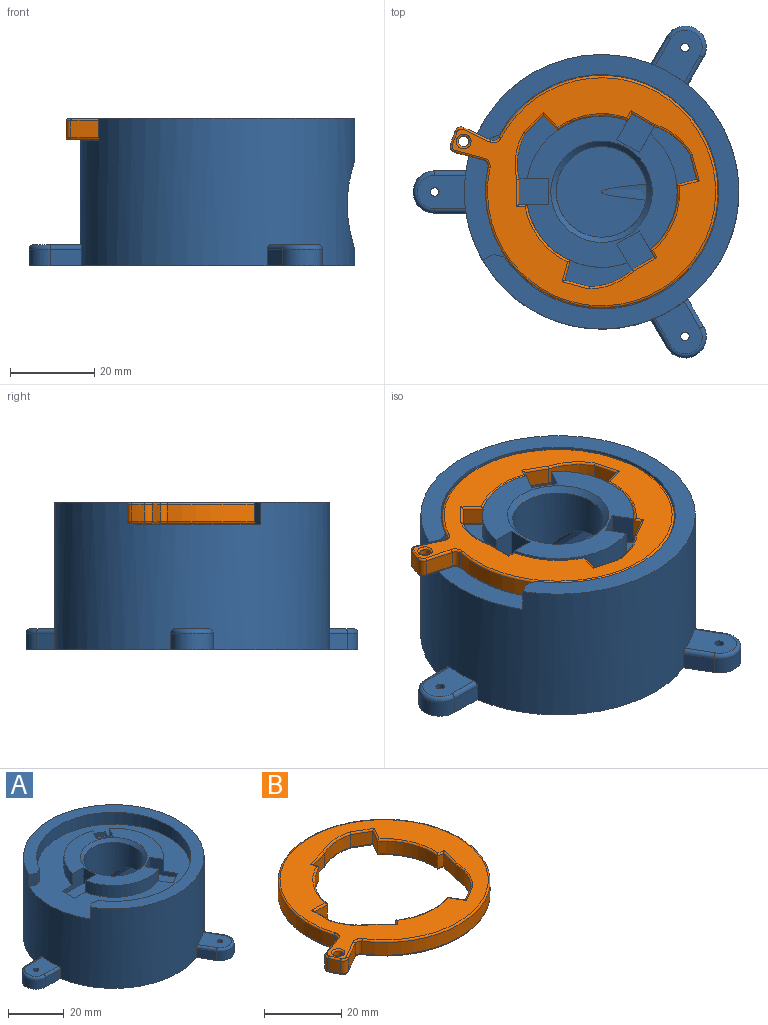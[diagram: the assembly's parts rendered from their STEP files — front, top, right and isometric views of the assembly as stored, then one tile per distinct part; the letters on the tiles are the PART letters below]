
ASSEMBLY  parts=2 mates=1
PART A: 58 faces, bbox 77.6x79.1x35 mm
  f0: plane 65x61.96mm, normal (0,0,1), area 758.2mm2, adj f8,f10,f54,f55,f56,f57
  f1: plane 35.8x35.53mm, normal (0,0,1), area 455.4mm2, adj f2,f3,f4,f9,f39,f40,f41,f44
  f2: cylinder r=17.9mm len=23.76mm, axis (0,0,1), area 162.5mm2, adj f1,f5,f46,f49
  f3: cylinder r=17.9mm len=23.76mm, axis (0,0,1), area 162.5mm2, adj f1,f5,f39,f51
  f4: cylinder r=17.9mm len=27.44mm, axis (0,0,1), area 162.5mm2, adj f1,f5,f41,f44
  f5: plane 60.25x55.5mm, normal (0,0,1), area 1457mm2, adj f2,f3,f4,f8,f10,f39,f41,f42
  f6: cylinder r=10.75mm len=28.75mm, axis (0,0,1), area 1605.1mm2, adj f7,f9,f36
  f7: plane 21.54x21.4mm, normal (0,0,1), area 337mm2, adj f6,f36,f37
  f8: cylinder r=32.5mm len=65mm, axis (0,0,-1), area 6482.6mm2, adj f0,f5,f20,f21,f22,f23,f24,f25
  f9: cone r=10.75mm half-angle=45deg, axis (0,0,1), area 126.3mm2, adj f1,f6
  f10: cylinder r=27.75mm len=55.5mm, axis (0,0,1), area 748.7mm2, adj f0,f5,f56,f57
  f11: torus R=4mm, axis (0,0,1), area 22.9mm2, adj f19,f21,f22,f23
  f12: torus R=4mm, axis (0,0,1), area 22.9mm2, adj f18,f26,f27,f28
  f13: torus R=4mm, axis (0,0,1), area 22.9mm2, adj f17,f31,f32,f33
  f14: cylinder r=1mm len=5mm, axis (0,0,-1), area 31.4mm2, adj f22,f35
  f15: cylinder r=1mm len=5mm, axis (0,0,-1), area 31.4mm2, adj f32,f35
  f16: cylinder r=1mm len=5mm, axis (0,0,-1), area 31.4mm2, adj f27,f35
  f17: cylinder r=5mm len=10mm, axis (0,0,-1), area 62.8mm2, adj f13,f30,f34,f35
  f18: cylinder r=5mm len=9.33mm, axis (0,0,-1), area 62.8mm2, adj f12,f25,f29,f35
  f19: cylinder r=5mm len=9.33mm, axis (0,0,-1), area 62.8mm2, adj f11,f20,f24,f35
  f20: plane 6.5x4mm, normal (-0.87,0.5,0), area 30mm2, adj f8,f19,f21,f35
  f21: cylinder r=1mm len=7mm, axis (0.5,0.87,0), area 11.7mm2, adj f8,f11,f20,f22
  f22: plane 12.37x11.14mm, normal (0,0,1), area 79.6mm2, adj f8,f11,f14,f21,f23
  f23: cylinder r=1mm len=7mm, axis (-0.5,-0.87,0), area 11.7mm2, adj f8,f11,f22,f24
  f24: plane 6.5x4mm, normal (0.87,-0.5,0), area 30mm2, adj f8,f19,f23,f35
  f25: plane 6.5x4mm, normal (0.87,0.5,0), area 30mm2, adj f8,f18,f26,f35
  f26: cylinder r=1mm len=7mm, axis (0.5,-0.87,0), area 11.7mm2, adj f8,f12,f25,f27
  f27: plane 12.37x11.14mm, normal (0,0,1), area 79.6mm2, adj f8,f12,f16,f26,f28
  f28: cylinder r=1mm len=7mm, axis (-0.5,0.87,0), area 11.7mm2, adj f8,f12,f27,f29
  f29: plane 6.5x4mm, normal (-0.87,-0.5,0), area 30mm2, adj f8,f18,f28,f35
  f30: plane 7.5x4mm, normal (0,-1,0), area 30mm2, adj f8,f17,f31,f35
  f31: cylinder r=1mm len=7.5mm, axis (-1,0,0), area 11.7mm2, adj f8,f13,f30,f32
  f32: plane 11.36x8mm, normal (0,0,1), area 79.6mm2, adj f8,f13,f15,f31,f33
  f33: cylinder r=1mm len=7.5mm, axis (1,0,0), area 11.7mm2, adj f8,f13,f32,f34
  f34: plane 7.5x4mm, normal (0,1,0), area 30mm2, adj f8,f17,f33,f35
  f35: plane 78.61x77.11mm, normal (0,0,-1), area 3643.9mm2, adj f8,f14,f15,f16,f17,f18,f19,f20
  f36: cone r=9.5mm half-angle=1deg, axis (1,0,0), area 1460.4mm2, adj f6,f7,f37,f38
  f37: cone r=9.5mm half-angle=1deg, axis (1,0,0), area 0mm2, adj f7,f36
  f38: bspline ~21.18x20.95mm, area 42.1mm2, adj f8,f36
  f39: plane 9.09x7mm, normal (0.87,-0.5,0), area 45.6mm2, adj f1,f3,f5,f40,f42,f43
  f40: plane 7x5.37mm, normal (0.5,0.87,0), area 43.4mm2, adj f1,f39,f41,f43
  f41: plane 9.09x7mm, normal (-0.87,0.5,0), area 45.6mm2, adj f1,f4,f5,f40,f42,f43
  f42: plane 5.37x3.1mm, normal (-0.5,-0.87,0), area 11.2mm2, adj f5,f39,f41,f43
  f43: plane 12.19x10.62mm, normal (0,0,1), area 65.1mm2, adj f39,f40,f41,f42
  f44: plane 9.09x7mm, normal (-0.87,-0.5,0), area 45.6mm2, adj f1,f4,f5,f45,f47,f48
  f45: plane 7x5.37mm, normal (0.5,-0.87,0), area 43.4mm2, adj f1,f44,f46,f48
  f46: plane 9.09x7mm, normal (0.87,0.5,0), area 45.6mm2, adj f1,f2,f5,f45,f47,f48
  f47: plane 5.37x3.1mm, normal (-0.5,0.87,0), area 11.2mm2, adj f5,f44,f46,f48
  f48: plane 12.19x10.62mm, normal (0,0,1), area 65.1mm2, adj f44,f45,f46,f47
  f49: plane 10.5x7mm, normal (0,1,0), area 45.6mm2, adj f1,f2,f5,f50,f52,f53
  f50: plane 7x6.2mm, normal (-1,0,0), area 43.4mm2, adj f1,f49,f51,f53
  f51: plane 10.5x7mm, normal (0,-1,0), area 45.6mm2, adj f1,f3,f5,f50,f52,f53
  f52: plane 6.2x1.8mm, normal (1,0,0), area 11.2mm2, adj f5,f49,f51,f53
  f53: plane 10.5x6.2mm, normal (0,0,1), area 65.1mm2, adj f49,f50,f51,f52
  f54: plane 5.2x2.55mm, normal (-0.42,-0.91,0), area 14.6mm2, adj f0,f5,f8,f56
  f55: plane 5.2x2.44mm, normal (-0.5,0.87,0), area 14.6mm2, adj f0,f5,f8,f57
  f56: plane 5.2x2.6mm, normal (0.31,-0.95,0), area 14.2mm2, adj f0,f5,f10,f54
  f57: plane 5.2x2.66mm, normal (0.23,0.97,0), area 14.2mm2, adj f0,f5,f10,f55
PART B: 83 faces, bbox 64.7x59.5x5 mm
  f0: cylinder r=15mm len=10.06mm, axis (0,0,-1), area 44.8mm2, adj f1,f24,f44,f71
  f1: plane 5.2x4mm, normal (-0.5,0.87,0), area 24mm2, adj f0,f2,f42,f69
  f2: plane 4.12x4mm, normal (0.87,0.5,0), area 19mm2, adj f1,f3,f40,f67
  f3: cylinder r=18mm len=16.67mm, axis (0,0,-1), area 70mm2, adj f2,f4,f38,f65
  f4: plane 4x1.3mm, normal (-0.71,0.71,0), area 7.4mm2, adj f3,f5,f36,f63
  f5: plane 4.24x4.24mm, normal (0.71,0.71,0), area 24mm2, adj f4,f6,f34,f61
  f6: cylinder r=15mm len=8.75mm, axis (0,0,-1), area 44.8mm2, adj f5,f7,f32,f59
  f7: plane 6x4mm, normal (1,0,0), area 24mm2, adj f6,f8,f30,f57
  f8: plane 4.75x4mm, normal (0,-1,0), area 19mm2, adj f7,f9,f29,f56
  f9: cylinder r=18mm len=13.35mm, axis (0,0,-1), area 70mm2, adj f8,f10,f31,f58
  f10: plane 4x1.78mm, normal (0.97,0.26,0), area 7.4mm2, adj f9,f11,f33,f60
  f11: plane 5.8x4mm, normal (0.26,-0.97,0), area 24mm2, adj f10,f12,f35,f62
  f12: cylinder r=15mm len=10.86mm, axis (0,0,-1), area 44.8mm2, adj f11,f13,f37,f64
  f13: plane 5.2x4mm, normal (-0.5,-0.87,0), area 24mm2, adj f12,f14,f39,f66
  f14: plane 4.12x4mm, normal (-0.87,0.5,0), area 19mm2, adj f13,f15,f41,f68
  f15: cylinder r=18mm len=15.53mm, axis (0,0,-1), area 70mm2, adj f14,f16,f43,f70
  f16: plane 4x1.78mm, normal (-0.26,-0.97,0), area 7.4mm2, adj f15,f24,f45,f72
  f17: cylinder r=1.5mm len=4mm, axis (0,0,-1), area 9.1mm2, adj f18,f25,f53,f80
  f18: plane 6.59x4mm, normal (-0.34,0.94,0), area 28mm2, adj f17,f19,f51,f78
  f19: cylinder r=1.5mm len=4mm, axis (0,0,-1), area 9.7mm2, adj f18,f20,f49,f76
  f20: cylinder r=37.5mm len=4mm, axis (0,0,-1), area 13.7mm2, adj f19,f21,f47,f74
  f21: cylinder r=1.5mm len=4mm, axis (0,0,-1), area 9.7mm2, adj f20,f22,f48,f75
  f22: plane 6.07x4mm, normal (0.5,-0.87,0), area 28mm2, adj f21,f23,f50,f77
  f23: cylinder r=1.5mm len=4mm, axis (0,0,-1), area 9.1mm2, adj f22,f25,f52,f79
  f24: plane 5.8x4mm, normal (-0.97,0.26,0), area 24mm2, adj f0,f16,f46,f73
  f25: cylinder r=27.5mm len=55mm, axis (0,0,-1), area 660.6mm2, adj f17,f23,f54,f81
  f26: cylinder r=1.25mm len=4mm, axis (0,0,-1), area 31.4mm2, adj f55,f82
  f27: plane 61.29x54mm, normal (0,0,1), area 1027.3mm2, adj f56,f57,f58,f59,f60,f61,f62,f63
  f28: plane 61.29x54mm, normal (0,0,-1), area 1027.3mm2, adj f29,f30,f31,f32,f33,f34,f35,f36
  f29: cylinder r=0.5mm len=5.25mm, axis (1,0,0), area 3.8mm2, adj f8,f28,f30,f31
  f30: cylinder r=0.5mm len=6.57mm, axis (0,1,0), area 4.9mm2, adj f7,f28,f29,f32
  f31: torus R=18.5mm, axis (0,0,1), area 13.6mm2, adj f9,f28,f29,f33
  f32: torus R=15.5mm, axis (0,0,1), area 8.9mm2, adj f6,f28,f30,f34
  f33: cylinder r=0.5mm len=2.39mm, axis (-0.26,0.97,0), area 1.5mm2, adj f10,f28,f31,f35
  f34: cylinder r=0.5mm len=4.95mm, axis (-0.71,0.71,0), area 4.8mm2, adj f5,f28,f32,f36
  f35: cylinder r=0.5mm len=6.41mm, axis (0.97,0.26,0), area 4.8mm2, adj f11,f28,f33,f37
  f36: cylinder r=0.5mm len=2.01mm, axis (-0.71,-0.71,0), area 1.5mm2, adj f4,f28,f34,f38
  f37: torus R=15.5mm, axis (0,0,1), area 8.9mm2, adj f12,f28,f35,f39
  f38: torus R=18.5mm, axis (0,0,1), area 13.6mm2, adj f3,f28,f36,f40
  f39: cylinder r=0.5mm len=5.94mm, axis (0.87,-0.5,0), area 4.9mm2, adj f13,f28,f37,f41
  f40: cylinder r=0.5mm len=4.8mm, axis (-0.5,0.87,0), area 3.8mm2, adj f2,f28,f38,f42
  f41: cylinder r=0.5mm len=4.8mm, axis (-0.5,-0.87,0), area 3.8mm2, adj f14,f28,f39,f43
  f42: cylinder r=0.5mm len=5.94mm, axis (-0.87,-0.5,0), area 4.9mm2, adj f1,f28,f40,f44
  f43: torus R=18.5mm, axis (0,0,1), area 13.6mm2, adj f15,f28,f41,f45
  f44: torus R=15.5mm, axis (0,0,1), area 8.9mm2, adj f0,f28,f42,f46
  f45: cylinder r=0.5mm len=2.39mm, axis (0.97,-0.26,0), area 1.5mm2, adj f16,f28,f43,f46
  f46: cylinder r=0.5mm len=6.41mm, axis (-0.26,-0.97,0), area 4.8mm2, adj f24,f28,f44,f45
  f47: torus R=37mm, axis (0,0,1), area 2.7mm2, adj f20,f28,f48,f49
  f48: torus R=1mm, axis (0,0,1), area 1.7mm2, adj f21,f28,f47,f50
  f49: torus R=1mm, axis (0,0,1), area 1.7mm2, adj f19,f28,f47,f51
  f50: cylinder r=0.5mm len=6.32mm, axis (0.87,0.5,0), area 5.5mm2, adj f22,f28,f48,f52
  f51: cylinder r=0.5mm len=6.76mm, axis (-0.94,-0.34,0), area 5.5mm2, adj f18,f28,f49,f53
  f52: torus R=2mm, axis (0,0,1), area 2mm2, adj f23,f28,f50,f54
  f53: torus R=2mm, axis (0,0,1), area 2mm2, adj f17,f28,f51,f54
  f54: torus R=27mm, axis (0,0,1), area 128.8mm2, adj f25,f28,f52,f53
  f55: torus R=1.75mm, axis (0,0,1), area 7.1mm2, adj f26,f28
  f56: cylinder r=0.5mm len=5.25mm, axis (-1,0,0), area 3.8mm2, adj f8,f27,f57,f58
  f57: cylinder r=0.5mm len=6.57mm, axis (0,-1,0), area 4.9mm2, adj f7,f27,f56,f59
  f58: torus R=18.5mm, axis (0,0,1), area 13.6mm2, adj f9,f27,f56,f60
  f59: torus R=15.5mm, axis (0,0,1), area 8.9mm2, adj f6,f27,f57,f61
  f60: cylinder r=0.5mm len=2.39mm, axis (0.26,-0.97,0), area 1.5mm2, adj f10,f27,f58,f62
  f61: cylinder r=0.5mm len=4.95mm, axis (0.71,-0.71,0), area 4.8mm2, adj f5,f27,f59,f63
  f62: cylinder r=0.5mm len=6.41mm, axis (-0.97,-0.26,0), area 4.8mm2, adj f11,f27,f60,f64
  f63: cylinder r=0.5mm len=2.01mm, axis (0.71,0.71,0), area 1.5mm2, adj f4,f27,f61,f65
  f64: torus R=15.5mm, axis (0,0,1), area 8.9mm2, adj f12,f27,f62,f66
  f65: torus R=18.5mm, axis (0,0,1), area 13.6mm2, adj f3,f27,f63,f67
  f66: cylinder r=0.5mm len=5.94mm, axis (-0.87,0.5,0), area 4.9mm2, adj f13,f27,f64,f68
  f67: cylinder r=0.5mm len=4.8mm, axis (0.5,-0.87,0), area 3.8mm2, adj f2,f27,f65,f69
  f68: cylinder r=0.5mm len=4.8mm, axis (0.5,0.87,0), area 3.8mm2, adj f14,f27,f66,f70
  f69: cylinder r=0.5mm len=5.94mm, axis (0.87,0.5,0), area 4.9mm2, adj f1,f27,f67,f71
  f70: torus R=18.5mm, axis (0,0,1), area 13.6mm2, adj f15,f27,f68,f72
  f71: torus R=15.5mm, axis (0,0,1), area 8.9mm2, adj f0,f27,f69,f73
  f72: cylinder r=0.5mm len=2.39mm, axis (-0.97,0.26,0), area 1.5mm2, adj f16,f27,f70,f73
  f73: cylinder r=0.5mm len=6.41mm, axis (0.26,0.97,0), area 4.8mm2, adj f24,f27,f71,f72
  f74: torus R=37mm, axis (0,0,1), area 2.7mm2, adj f20,f27,f75,f76
  f75: torus R=1mm, axis (0,0,1), area 1.7mm2, adj f21,f27,f74,f77
  f76: torus R=1mm, axis (0,0,1), area 1.7mm2, adj f19,f27,f74,f78
  f77: cylinder r=0.5mm len=6.32mm, axis (-0.87,-0.5,0), area 5.5mm2, adj f22,f27,f75,f79
  f78: cylinder r=0.5mm len=6.76mm, axis (0.94,0.34,0), area 5.5mm2, adj f18,f27,f76,f80
  f79: torus R=2mm, axis (0,0,1), area 2mm2, adj f23,f27,f77,f81
  f80: torus R=2mm, axis (0,0,1), area 2mm2, adj f17,f27,f78,f81
  f81: torus R=27mm, axis (0,0,1), area 128.8mm2, adj f25,f27,f79,f80
  f82: torus R=1.75mm, axis (0,0,1), area 7.1mm2, adj f26,f27
PLACE A t=(22.37,-95.21,-54.95)mm
PLACE B rot(axis=(0,0,-1),45deg) t=(22.37,-95.21,-25.05)mm
MATE revolute B.f9 <-> A.f2  axis (0,0,-1) through (22.37,-95.21,-22.55)mm
